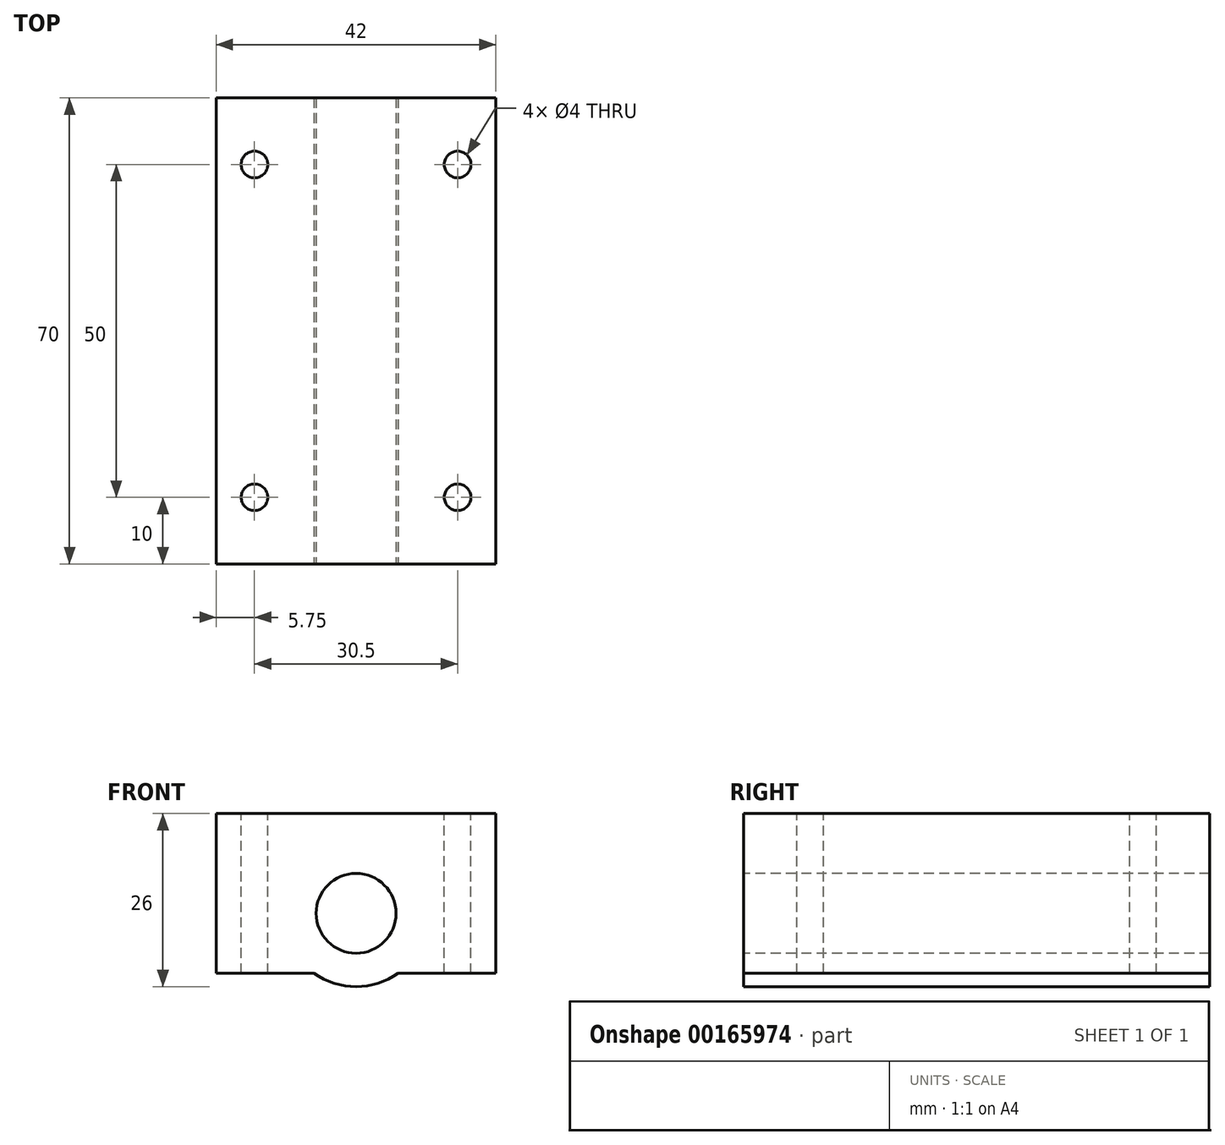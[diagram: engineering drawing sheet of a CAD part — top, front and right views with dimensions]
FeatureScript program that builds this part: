
annotation { "Feature Type Name" : "Feature", "Feature Type Description" : "" }
export const myFeature = defineFeature(function(context is Context, id is Id, definition is map)
    precondition{}
    {
        {
            var Q0;
            Q0=qCreatedBy(makeId("Front.planeOp"),FACE);
            var sketch = newSketch(context, id + "F0", { "sketchPlane" : qUnion([Q0])});
            skCircle(sketch, "E0", {"center": v(0, 0) * mm, "radius": 6 * mm});
            skLineSegment(sketch, "E1.bottom", {"start": v(-21, 15) * mm, "end": v(21, 15) * mm});
            skLineSegment(sketch, "E1.top", {"start": v(-21, -9) * mm, "end": v(-6.32, -9) * mm});
            skLineSegment(sketch, "E1.left", {"start": v(-21, 15) * mm, "end": v(-21, -9) * mm});
            skLineSegment(sketch, "E1.right", {"start": v(21, 15) * mm, "end": v(21, -9) * mm});
            skArc(sketch, "E2", {"start": v(-6.32, -9) * mm, "mid": v(0, -11) * mm, "end": v(6.32, -9) * mm});
            skLineSegment(sketch, "E3.trimOffspring", {"start": v(6.32, -9) * mm, "end": v(21, -9) * mm});
            skSolve(sketch);
        }
        {
            var Q0;
            Q0 = qSketchRegion(id + "F0", true);
            extrude(context, id + "F1", {"entities" : qUnion([Q0]), "oppositeDirection" : true, "depth" : 70 * mm});
        }
        {
            var Q0;
            Q0=makeQuery(id+"F1.opExtrude","SWEPT_FACE",FACE,{"disambiguationData":[OSD([sQuery(id+"F0.wireOp",EDGE,"E1.bottom")])]});
            var sketch = newSketch(context, id + "F2", { "sketchPlane" : qUnion([Q0])});
            skCircle(sketch, "E4", {"center": v(-15.25, 10) * mm, "radius": 2 * mm});
            skLineSegment(sketch, "E5", {"start": v(-21, 35) * mm, "end": v(21, 35) * mm, "construction": true});
            skCircle(sketch, "E6.MirrorC", {"center": v(-15.25, 60) * mm, "radius": 2 * mm});
            skCircle(sketch, "E7.MirrorC", {"center": v(15.25, 60) * mm, "radius": 2 * mm});
            skCircle(sketch, "E8.MirrorC", {"center": v(15.25, 10) * mm, "radius": 2 * mm});
            skSolve(sketch);
        }
        {
            var Q0;
            Q0 = qSketchRegion(id + "F2", true);
            extrude(context, id + "F3", {"entities" : qUnion([Q0]), "operationType" : NewBodyOperationType.REMOVE, "endBound" : BoundingType.THROUGH_ALL, "oppositeDirection" : true, "depth" : 25 * mm});
        }
    });
